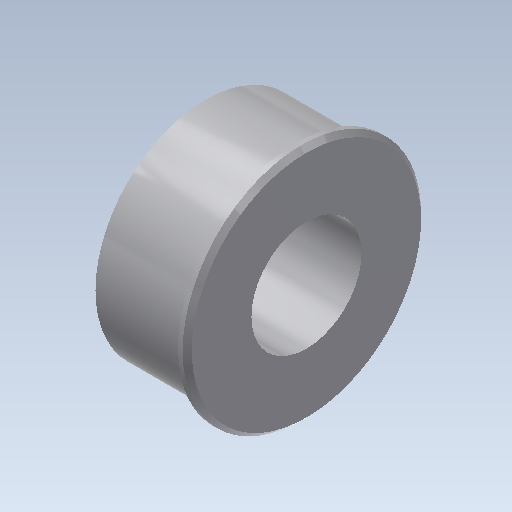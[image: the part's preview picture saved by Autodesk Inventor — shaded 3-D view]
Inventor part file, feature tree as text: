
AUTODESK INVENTOR PART (.ipt)
format: ipt  version: 2020 (Build 240168000, 168)  size: 124,416 bytes
history: native  units: mm
features: extrude x3, sketch x3, chamfer x1
ambient origin geometry x8: Origin, YZ Plane, XZ Plane, XY Plane, X Axis, Y Axis, Z Axis, Center Point
bodies: Solid1 (feature_tree)
feature tree (7):
  extrude  "Extrusion1"  Depth=5.0mm TaperAngle=0.0deg
  extrude  "Extrusion2"  Depth=0.5mm TaperAngle=0.0deg
  chamfer  "Chamfer1"  Distance=0.25mm Angle=45.0deg
  extrude  "Extrusion3"  Depth=5.0mm TaperAngle=0.0deg
  sketch  "Sketch1"  dims[d0=12.0mm d1=5.0mm d2=0.0mm]
  sketch  "Sketch2"  dims[d3=13.0mm d4=0.5mm d5=0.0mm d6=0.25mm d7=2.0mm d8=45.0deg]
  sketch  "Sketch3"  dims[d9=6.0mm d10=5.0mm d11=0.0mm]
